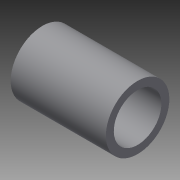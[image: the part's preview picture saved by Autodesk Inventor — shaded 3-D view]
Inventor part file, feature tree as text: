
AUTODESK INVENTOR PART (.ipt)
format: ipt  version: 2015 SP1 (Build 190203100, 203)  size: 81,920 bytes
history: native  units: in
note: dims shown in document units (in); Inventor stores cm internally (conversion verified against a paired STEP export)
features: extrude x1, sketch x1
ambient origin geometry x8: Origin, YZ Plane, XZ Plane, XY Plane, X Axis, Y Axis, Z Axis, Center Point
bodies: Solid1 (feature_tree)
feature tree (2):
  extrude  "Extrusion1"  Depth=0.75in
  sketch  "Sketch1"  dims[d0=0.375in d1=0.5in d2=0.75in d3=0.0in]
